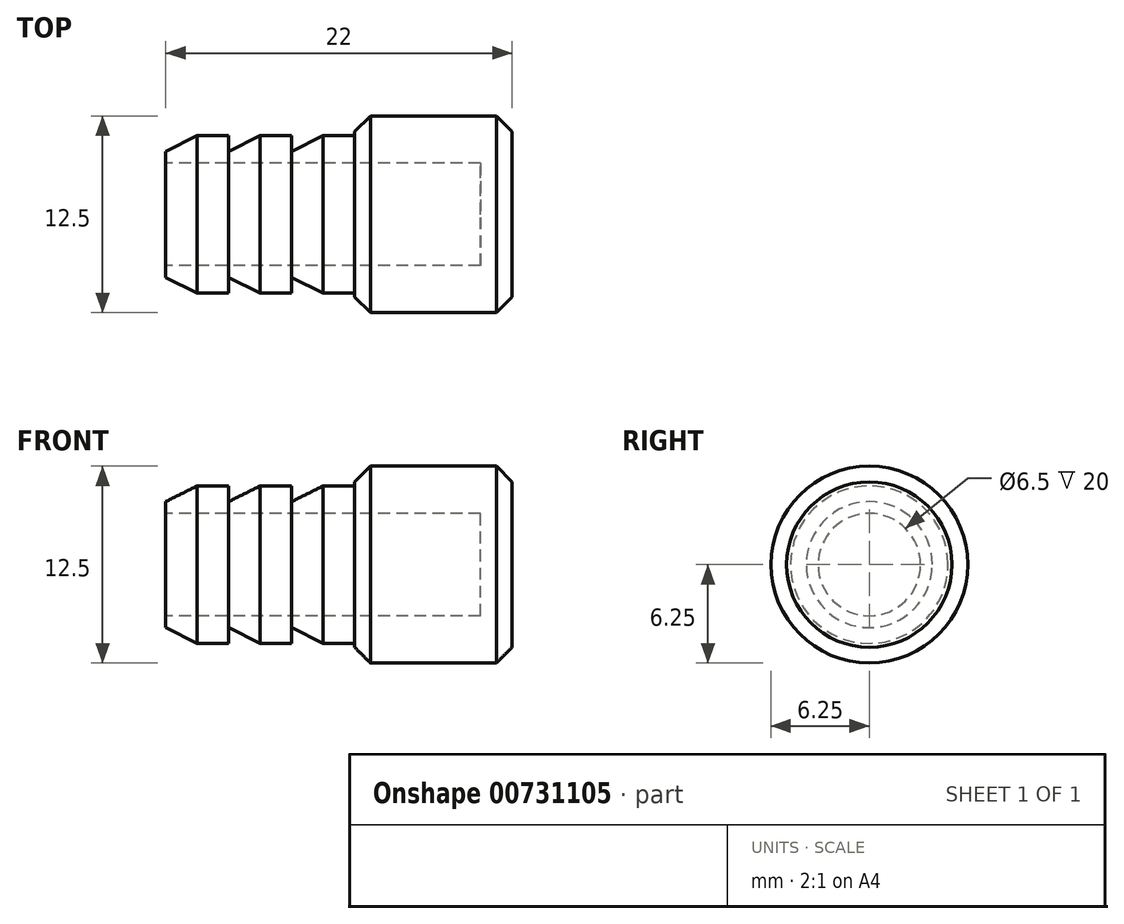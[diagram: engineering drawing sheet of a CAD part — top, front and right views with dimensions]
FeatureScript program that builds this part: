
annotation { "Feature Type Name" : "Feature", "Feature Type Description" : "" }
export const myFeature = defineFeature(function(context is Context, id is Id, definition is map)
    precondition{}
    {
        {
            var Q0;
            Q0=qCreatedBy(makeId("Right.planeOp"),FACE);
            var sketch = newSketch(context, id + "F0", { "sketchPlane" : qUnion([Q0])});
            skCircle(sketch, "E0", {"center": v(0, 0) * mm, "radius": 6.25 * mm});
            skCircle(sketch, "E1", {"center": v(0, 0) * mm, "radius": 3.25 * mm});
            skSolve(sketch);
        }
        {
            var Q0;
            Q0 = qSketchRegion(id + "F0", true);
            extrude(context, id + "F1", {"entities" : qUnion([Q0]), "depth" : 10 * mm, "offsetDistance" : 25 * mm});
        }
        {
            var Q0;
            Q0=makeQuery(id+"F1.opExtrude","CAP_FACE",FACE,{"disambiguationData":[OSD([sQuery(id+"F0.wireOp",EDGE,"E0"),sQuery(id+"F0.wireOp",EDGE,"E1")])],"isStart":true});
            var sketch = newSketch(context, id + "F2", { "sketchPlane" : qUnion([Q0])});
            skCircle(sketch, "E2", {"center": v(0, 0) * mm, "radius": 5 * mm});
            skCircle(sketch, "E3", {"center": v(0, 0) * mm, "radius": 3.25 * mm});
            skSolve(sketch);
        }
        {
            var Q0;
            Q0 = qSketchRegion(id + "F2", true);
            extrude(context, id + "F3", {"entities" : qUnion([Q0]), "operationType" : NewBodyOperationType.ADD, "depth" : 12 * mm, "offsetDistance" : 25 * mm});
        }
        {
            var Q0;
            Q0=qCreatedBy(makeId("Front.planeOp"),FACE);
            var sketch = newSketch(context, id + "F4", { "sketchPlane" : qUnion([Q0])});
            skLineSegment(sketch, "E4", {"start": v(-12, 5) * mm, "end": v(-10, 5) * mm});
            skLineSegment(sketch, "E5", {"start": v(-10, 5) * mm, "end": v(-12, 4) * mm});
            skLineSegment(sketch, "E6", {"start": v(-12, 4) * mm, "end": v(-12, 5) * mm});
            skLineSegment(sketch, "E7", {"start": v(-6, 5) * mm, "end": v(-8, 5) * mm});
            skLineSegment(sketch, "E8", {"start": v(-8, 5) * mm, "end": v(-8, 4) * mm});
            skLineSegment(sketch, "E9", {"start": v(-8, 4) * mm, "end": v(-6, 5) * mm});
            skLineSegment(sketch, "E10", {"start": v(-2, 5) * mm, "end": v(-4, 4) * mm});
            skLineSegment(sketch, "E11", {"start": v(-4, 4) * mm, "end": v(-4, 5) * mm});
            skLineSegment(sketch, "E12", {"start": v(-4, 5) * mm, "end": v(-2, 5) * mm});
            skLineSegment(sketch, "E13", {"start": v(0, 0) * mm, "end": v(-20, 0) * mm});
            skSolve(sketch);
        }
        {
            var Q0;
            Q0 = qSketchRegion(id + "F4", true);
            var Q1;
            Q1=sQuery(id+"F4.wireOp",EDGE,"E13");
            revolve(context, id + "F5", {"operationType" : NewBodyOperationType.REMOVE, "surfaceOperationType" : NewSurfaceOperationType.NEW, "entities" : qUnion([Q0]), "axis" : qUnion([Q1]), "revolveType" : RevolveType.FULL, "oppositeDirection" : true});
        }
        {
            var Q0;
            Q0=makeQuery(id+"F1.opExtrude","CAP_FACE",FACE,{"disambiguationData":[OSD([sQuery(id+"F0.wireOp",EDGE,"E0"),sQuery(id+"F0.wireOp",EDGE,"E1")])],"isStart":false});
            var sketch = newSketch(context, id + "F6", { "sketchPlane" : qUnion([Q0])});
            skCircle(sketch, "E14", {"center": v(0, 0) * mm, "radius": 6.25 * mm});
            skSolve(sketch);
        }
        {
            var Q0;
            Q0 = qSketchRegion(id + "F6", true);
            extrude(context, id + "F7", {"entities" : qUnion([Q0]), "operationType" : NewBodyOperationType.ADD, "oppositeDirection" : true, "depth" : 2 * mm, "offsetDistance" : 25 * mm});
        }
        {
            var Q0;
            Q0=makeQuery(id+"F1.opExtrude","CAP_EDGE",EDGE,{"disambiguationData":[OSD([sQuery(id+"F0.wireOp",EDGE,"E0")])],"isStart":false});
            var Q1;
            Q1=makeQuery(id+"F1.opExtrude","CAP_EDGE",EDGE,{"disambiguationData":[OSD([sQuery(id+"F0.wireOp",EDGE,"E0")])],"isStart":true});
            chamfer(context, id + "F8", {"entities" : qUnion([Q0, Q1]), "width" : 1 * mm, "tangentPropagation" : true});
        }
    });
